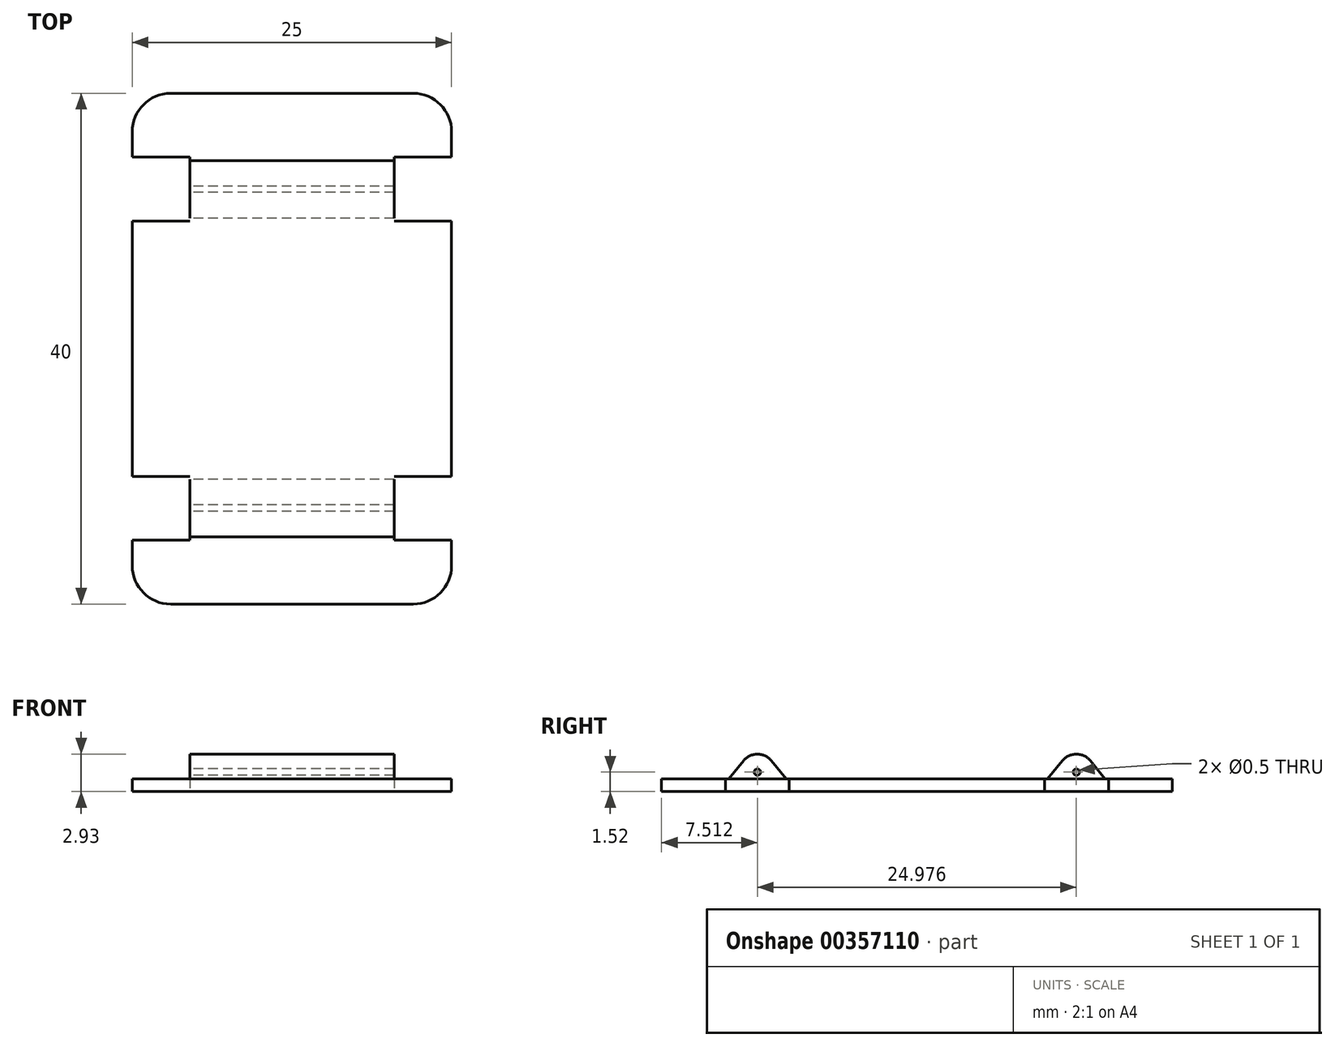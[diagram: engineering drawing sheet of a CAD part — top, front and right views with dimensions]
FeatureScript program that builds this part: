
annotation { "Feature Type Name" : "Feature", "Feature Type Description" : "" }
export const myFeature = defineFeature(function(context is Context, id is Id, definition is map)
    precondition{}
    {
        {
            var Q0;
            Q0=qCreatedBy(makeId("Top.planeOp"),FACE);
            var sketch = newSketch(context, id + "F0", { "sketchPlane" : qUnion([Q0])});
            skLineSegment(sketch, "E0.bottom", {"start": v(9.5, 20) * mm, "end": v(-9.5, 20) * mm});
            skLineSegment(sketch, "E0.top", {"start": v(9.5, -20) * mm, "end": v(-9.5, -20) * mm});
            skLineSegment(sketch, "E0.left", {"start": v(12.5, 17) * mm, "end": v(12.5, 15) * mm});
            skLineSegment(sketch, "E0.right", {"start": v(-12.5, 17) * mm, "end": v(-12.5, 15) * mm});
            skPoint(sketch, "E0.middle", {"position": v(0, 0) * mm});
            skLineSegment(sketch, "E1.bottom", {"start": v(-12.5, 15) * mm, "end": v(-8, 15) * mm});
            skLineSegment(sketch, "E1.top", {"start": v(-12.5, 10) * mm, "end": v(-8, 10) * mm});
            skLineSegment(sketch, "E1.right", {"start": v(-8, 15) * mm, "end": v(-8, 10) * mm});
            skLineSegment(sketch, "E2.MirrorCS", {"start": v(12.5, 15) * mm, "end": v(8, 15) * mm});
            skLineSegment(sketch, "E3.MirrorCS", {"start": v(8, 15) * mm, "end": v(8, 10) * mm});
            skLineSegment(sketch, "E4.MirrorCS", {"start": v(12.5, 10) * mm, "end": v(8, 10) * mm});
            skLineSegment(sketch, "E5.MirrorCS", {"start": v(-12.5, -15) * mm, "end": v(-8, -15) * mm});
            skLineSegment(sketch, "E6.MirrorCS", {"start": v(-12.5, -10) * mm, "end": v(-8, -10) * mm});
            skLineSegment(sketch, "E7.MirrorCS", {"start": v(-8, -15) * mm, "end": v(-8, -10) * mm});
            skLineSegment(sketch, "E8.MirrorCS", {"start": v(8, -15) * mm, "end": v(8, -10) * mm});
            skLineSegment(sketch, "E9.MirrorCS", {"start": v(12.5, -15) * mm, "end": v(8, -15) * mm});
            skLineSegment(sketch, "E10.MirrorCS", {"start": v(12.5, -10) * mm, "end": v(8, -10) * mm});
            skLineSegment(sketch, "E11.trimOffspring", {"start": v(12.5, 10) * mm, "end": v(12.5, -10) * mm});
            skLineSegment(sketch, "E12.trimOffspring", {"start": v(-12.5, 10) * mm, "end": v(-12.5, -10) * mm});
            skLineSegment(sketch, "E13.trimOffspring", {"start": v(-12.5, -15) * mm, "end": v(-12.5, -17) * mm});
            skLineSegment(sketch, "E14.trimOffspring", {"start": v(12.5, -15) * mm, "end": v(12.5, -17) * mm});
            skPoint(sketch, "E15.visualSharp", {"position": v(-12.5, 20) * mm});
            skArc(sketch, "E15.filletArc", {"start": v(-9.5, 20) * mm, "mid": v(-11.62, 19.12) * mm, "end": v(-12.5, 17) * mm});
            skPoint(sketch, "E16.visualSharp", {"position": v(12.5, 20) * mm});
            skArc(sketch, "E16.filletArc", {"start": v(12.5, 17) * mm, "mid": v(11.62, 19.12) * mm, "end": v(9.5, 20) * mm});
            skPoint(sketch, "E17.visualSharp", {"position": v(12.5, -20) * mm});
            skArc(sketch, "E17.filletArc", {"start": v(9.5, -20) * mm, "mid": v(11.62, -19.12) * mm, "end": v(12.5, -17) * mm});
            skPoint(sketch, "E18.visualSharp", {"position": v(-12.5, -20) * mm});
            skArc(sketch, "E18.filletArc", {"start": v(-12.5, -17) * mm, "mid": v(-11.62, -19.12) * mm, "end": v(-9.5, -20) * mm});
            skSolve(sketch);
        }
        {
            var Q0;
            Q0 = qSketchRegion(id + "F0", true);
            extrude(context, id + "F1", {"entities" : qUnion([Q0]), "depth" : 1 * mm});
        }
        {
            var Q0;
            Q0=qCreatedBy(makeId("Right.planeOp"),FACE);
            var sketch = newSketch(context, id + "F2", { "sketchPlane" : qUnion([Q0])});
            skArc(sketch, "E19", {"start": v(13.57, 2.42) * mm, "mid": v(12.49, 2.93) * mm, "end": v(11.4, 2.42) * mm});
            skLineSegment(sketch, "E20", {"start": v(14.74, 1) * mm, "end": v(13.57, 2.42) * mm});
            skLineSegment(sketch, "E21", {"start": v(11.4, 2.42) * mm, "end": v(10.22, 0.99) * mm});
            skPoint(sketch, "E22.orphan", {"position": v(11.19, 0.99) * mm});
            skCircle(sketch, "E23", {"center": v(12.49, 1.52) * mm, "radius": 0.25 * mm});
            skLineSegment(sketch, "E24.MirrorCS", {"start": v(-11.4, 2.42) * mm, "end": v(-10.22, 0.99) * mm});
            skArc(sketch, "E25.MirrorCS", {"start": v(-13.57, 2.42) * mm, "mid": v(-12.49, 2.93) * mm, "end": v(-11.4, 2.42) * mm});
            skLineSegment(sketch, "E26.MirrorCS", {"start": v(-14.74, 1) * mm, "end": v(-13.57, 2.42) * mm});
            skCircle(sketch, "E27.MirrorC", {"center": v(-12.49, 1.52) * mm, "radius": 0.25 * mm});
            skLineSegment(sketch, "E28", {"start": v(14.74, 1) * mm, "end": v(10.22, 0.99) * mm});
            skLineSegment(sketch, "E29", {"start": v(-14.74, 1) * mm, "end": v(-10.22, 0.99) * mm});
            skSolve(sketch);
        }
        {
            var Q0;
            Q0=makeQuery(id+"F2.imprint","IMPRINT",FACE,{"disambiguationData":[TD([[makeQuery(id+"F2.imprint","IMPRINT",EDGE,{"derivedFrom":sQuery(id+"F2.wireOp",EDGE,"E19")}),1.0]])]});
            var Q1;
            Q1=makeQuery(id+"F2.imprint","IMPRINT",FACE,{"disambiguationData":[TD([[makeQuery(id+"F2.imprint","IMPRINT",EDGE,{"derivedFrom":sQuery(id+"F2.wireOp",EDGE,"E24.MirrorCS")}),-1.0]])]});
            extrude(context, id + "F3", {"entities" : qUnion([Q0, Q1]), "endBound" : BoundingType.SYMMETRIC, "depth" : 16 * mm});
        }
    });
